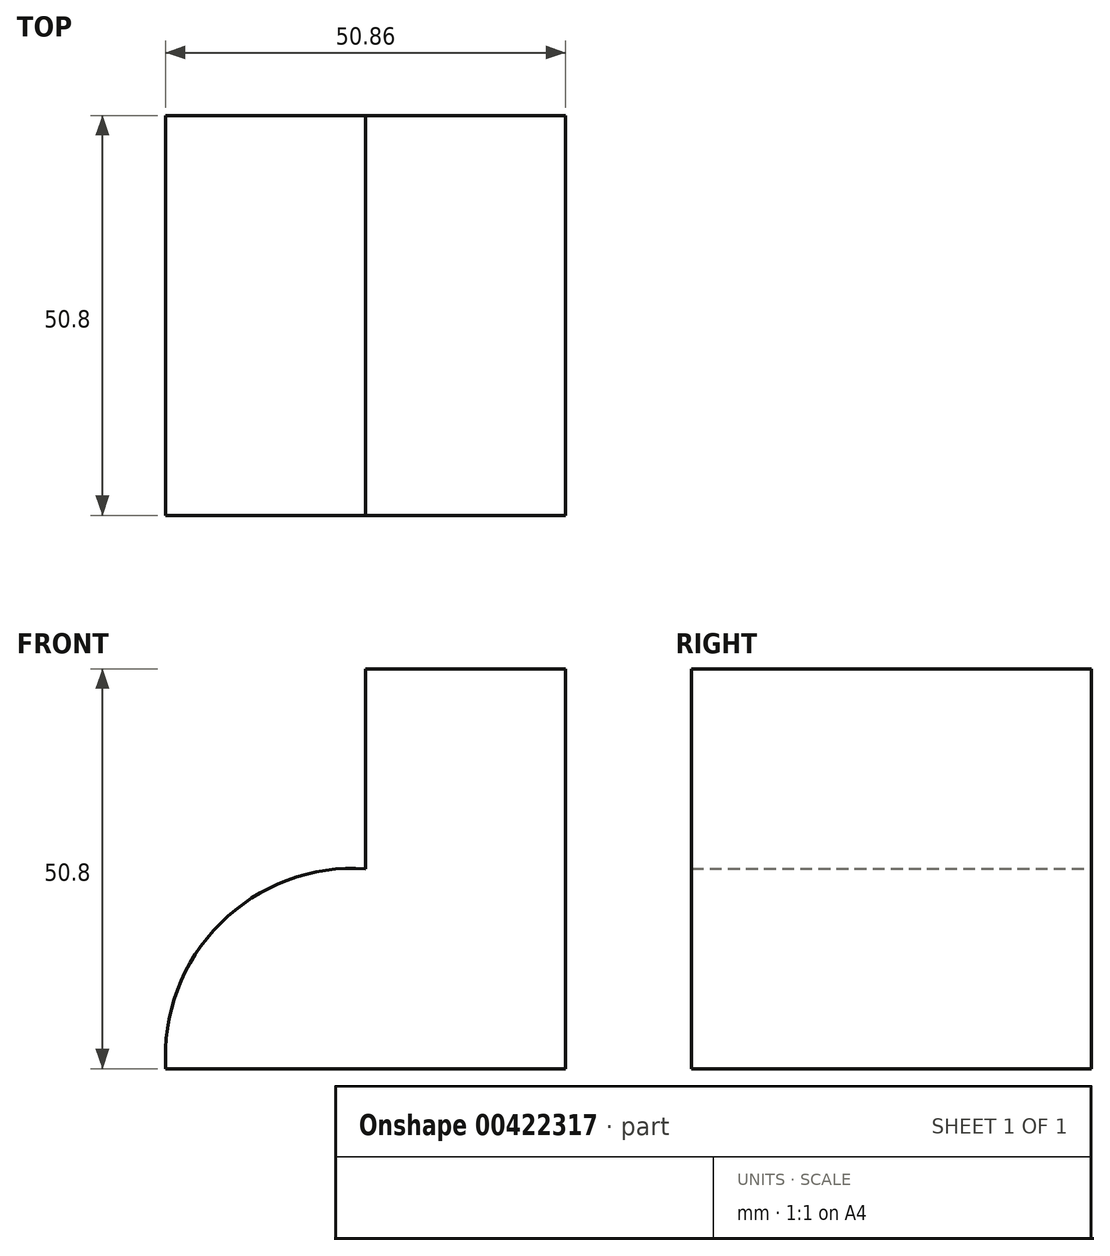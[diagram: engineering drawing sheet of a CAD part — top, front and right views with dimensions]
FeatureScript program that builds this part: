
annotation { "Feature Type Name" : "Feature", "Feature Type Description" : "" }
export const myFeature = defineFeature(function(context is Context, id is Id, definition is map)
    precondition{}
    {
        {
            var Q0;
            Q0=qCreatedBy(makeId("Front.planeOp"),FACE);
            var sketch = newSketch(context, id + "F0", { "sketchPlane" : qUnion([Q0])});
            skLineSegment(sketch, "E0", {"start": v(-25.4, 50.8) * mm, "end": v(0, 50.8) * mm});
            skLineSegment(sketch, "E1", {"start": v(0, 50.8) * mm, "end": v(0, 0) * mm});
            skLineSegment(sketch, "E2", {"start": v(0, 0) * mm, "end": v(-50.8, 0) * mm});
            skLineSegment(sketch, "E3", {"start": v(-25.4, 50.8) * mm, "end": v(-25.4, 25.4) * mm});
            skArc(sketch, "E4", {"start": v(-25.4, 25.4) * mm, "mid": v(-43.87, 18.47) * mm, "end": v(-50.8, 0) * mm});
            skSolve(sketch);
        }
        {
            var Q0;
            Q0=makeQuery(id+"F0.imprint","IMPRINT",FACE,{"disambiguationData":[TD([[makeQuery(id+"F0.imprint","IMPRINT",EDGE,{"derivedFrom":sQuery(id+"F0.wireOp",EDGE,"E0")}),-1.0]])]});
            extrude(context, id + "F1", {"entities" : qUnion([Q0]), "depth" : 50.8 * mm});
        }
    });
